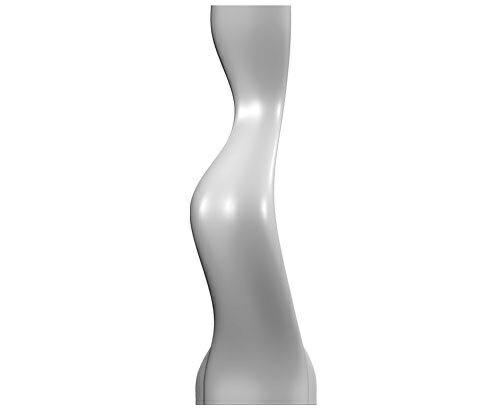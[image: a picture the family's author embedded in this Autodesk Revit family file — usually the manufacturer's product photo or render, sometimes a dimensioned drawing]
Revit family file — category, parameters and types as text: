
# Revit family: CITY ALPHABET letter „I”
name_source: partatom
category: Furniture
revit_build: Autodesk Revit 2018 (Build: 20190510_1515(x64)
units: mm (PartAtom-declared; Revit-internal decimal feet)

## family parameters
Cut with Voids When Loaded = No
Host = Face
OmniClass Number = 23.40.10.11.14
OmniClass Title = Exterior Seating
Room Calculation Point = No
Shared = No

## types (1)
- CITY ALPHABET letter „I”
    Default Elevation = 1219 mm
    Height = 590 mm  [stored 1.9357 ft]
    IfcExportAs = IfcFurnishingElement
    Length = 760 mm
    Manufacturer = Astrini Design
    Material information = Colour choice from RAL colour standard. Customer may inquire about specific request regarding individual order.
    Model = CITY ALPHABET letter „I”
    Operating temperature = -40°C to 80°C, ( -40°F to 176°F )
    Type Comments = Bench
    Type Image = I.jpg
    URL = https://astrini-design.pl
    Weight (approximately) = 35.00 kg
    Weight - filled (approximately) = 85.00 kg
    Width = 2400 mm

note: [stored X ft] marks values corroborated as IEEE doubles in the binary element streams (Revit-internal decimal feet)
